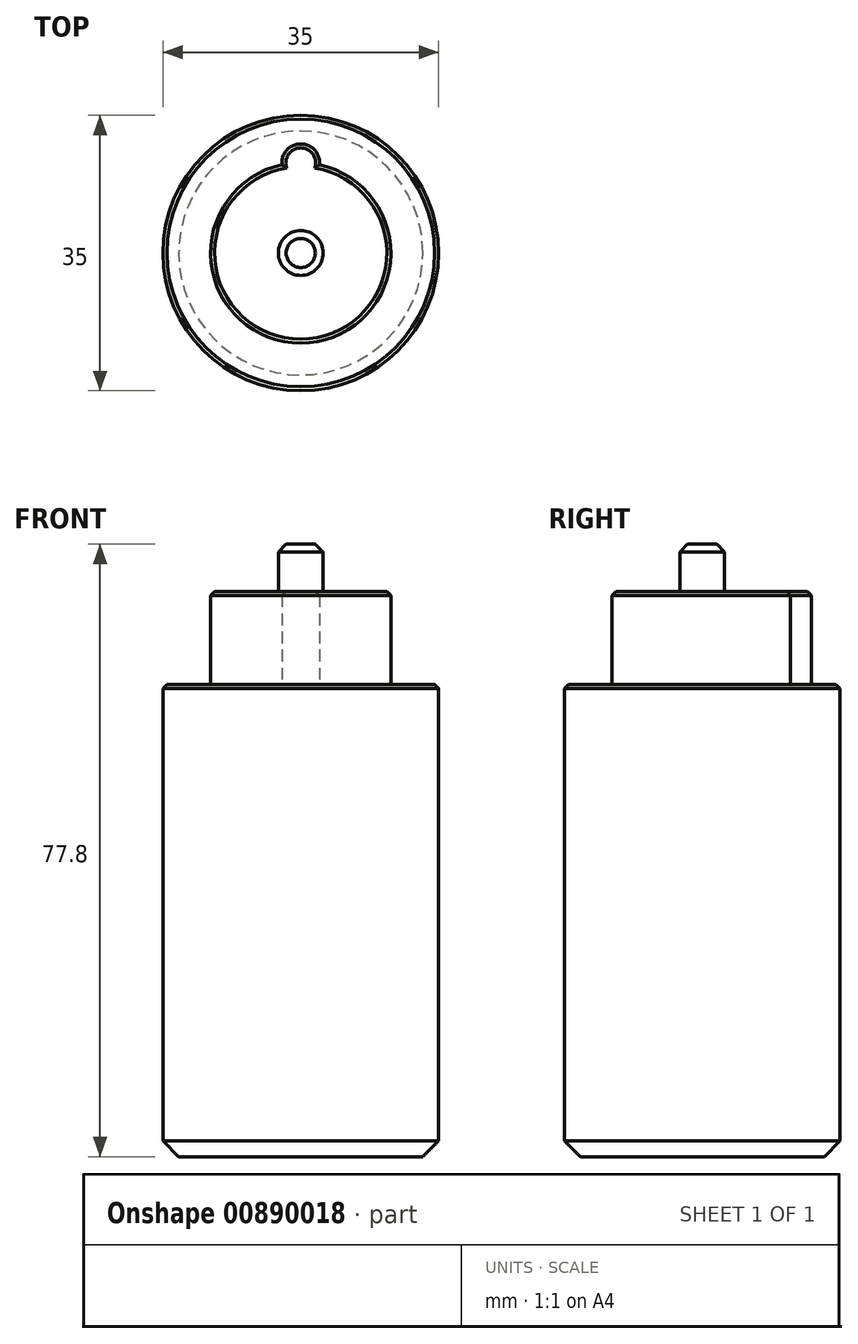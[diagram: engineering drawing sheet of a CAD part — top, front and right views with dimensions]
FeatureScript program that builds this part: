
annotation { "Feature Type Name" : "Feature", "Feature Type Description" : "" }
export const myFeature = defineFeature(function(context is Context, id is Id, definition is map)
    precondition{}
    {
        {
            var Q0;
            Q0=qCreatedBy(makeId("Top.planeOp"),FACE);
            var sketch = newSketch(context, id + "F0", { "sketchPlane" : qUnion([Q0])});
            skCircle(sketch, "E0", {"center": v(0, 0) * mm, "radius": 17.5 * mm});
            skSolve(sketch);
        }
        {
            var Q0;
            Q0 = qSketchRegion(id + "F0", true);
            extrude(context, id + "F1", {"entities" : qUnion([Q0]), "depth" : 60 * mm, "offsetDistance" : 25 * mm});
        }
        {
            var Q0;
            Q0=makeQuery(id+"F1.opExtrude","CAP_FACE",FACE,{"disambiguationData":[OSD([sQuery(id+"F0.wireOp",EDGE,"E0")])],"isStart":false});
            var sketch = newSketch(context, id + "F2", { "sketchPlane" : qUnion([Q0])});
            skCircle(sketch, "E1", {"center": v(0, 0) * mm, "radius": 11.45 * mm});
            skCircle(sketch, "E2", {"center": v(0, 11.45) * mm, "radius": 2.4 * mm});
            skSolve(sketch);
        }
        {
            var Q0;
            Q0 = qSketchRegion(id + "F2", true);
            extrude(context, id + "F3", {"entities" : qUnion([Q0]), "operationType" : NewBodyOperationType.ADD, "depth" : 11.8 * mm, "offsetDistance" : 25 * mm});
        }
        {
            var Q0;
            Q0=makeQuery(id+"F3.opExtrude","CAP_FACE",FACE,{"disambiguationData":[OSD([sQuery(id+"F2.wireOp",EDGE,"E1"),sQuery(id+"F2.wireOp",EDGE,"E2")])],"isStart":false});
            var sketch = newSketch(context, id + "F4", { "sketchPlane" : qUnion([Q0])});
            skCircle(sketch, "E3", {"center": v(0, 0) * mm, "radius": 2.85 * mm});
            skSolve(sketch);
        }
        {
            var Q0;
            Q0 = qSketchRegion(id + "F4", true);
            extrude(context, id + "F5", {"entities" : qUnion([Q0]), "operationType" : NewBodyOperationType.ADD, "depth" : 6 * mm, "offsetDistance" : 25 * mm});
        }
        {
            var Q0;
            Q0=makeQuery(id+"F5.opExtrude","CAP_EDGE",EDGE,{"disambiguationData":[OSD([sQuery(id+"F4.wireOp",EDGE,"E3")])],"isStart":false});
            chamfer(context, id + "F6", {"entities" : qUnion([Q0]), "width" : 1 * mm, "tangentPropagation" : true});
        }
        {
            var Q0;
            Q0=makeQuery(id+"F3.opExtrude","CAP_EDGE",EDGE,{"disambiguationData":[OSD([sQuery(id+"F2.wireOp",EDGE,"E1")])],"isStart":false});
            var Q1;
            Q1=makeQuery(id+"F3.opExtrude","CAP_EDGE",EDGE,{"disambiguationData":[OSD([sQuery(id+"F2.wireOp",EDGE,"E2")])],"isStart":false});
            var Q2;
            Q2=makeQuery(id+"F1.opExtrude","CAP_EDGE",EDGE,{"disambiguationData":[OSD([sQuery(id+"F0.wireOp",EDGE,"E0")])],"isStart":false});
            chamfer(context, id + "F7", {"entities" : qUnion([Q0, Q1, Q2]), "width" : .5 * mm, "tangentPropagation" : true});
        }
        {
            var Q0;
            Q0=makeQuery(id+"F1.opExtrude","CAP_FACE",FACE,{"disambiguationData":[OSD([sQuery(id+"F0.wireOp",EDGE,"E0")])],"isStart":true});
            chamfer(context, id + "F8", {"entities" : qUnion([Q0]), "width" : 2 * mm, "tangentPropagation" : true});
        }
    });
